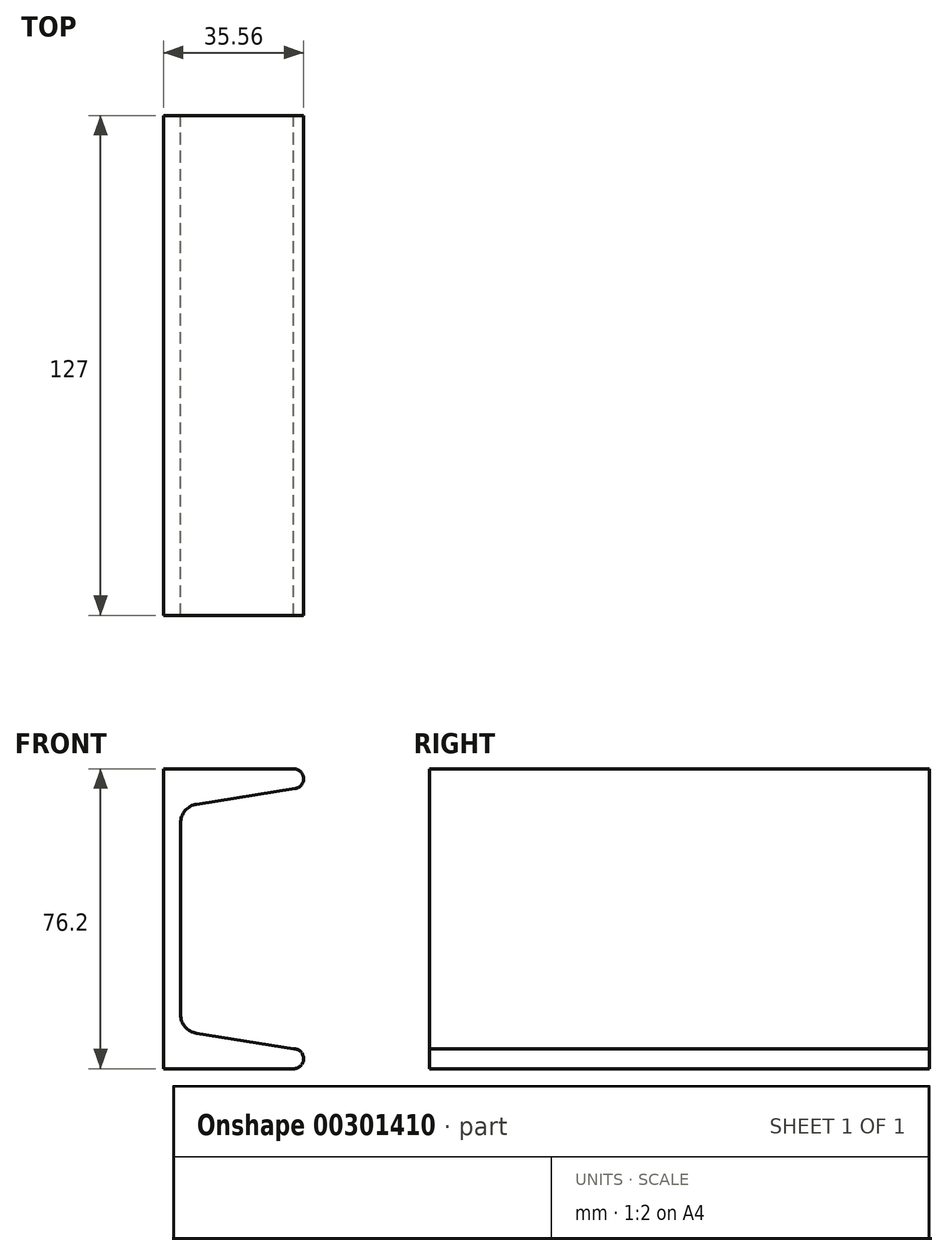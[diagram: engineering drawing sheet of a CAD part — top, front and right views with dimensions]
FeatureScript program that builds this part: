
annotation { "Feature Type Name" : "Feature", "Feature Type Description" : "" }
export const myFeature = defineFeature(function(context is Context, id is Id, definition is map)
    precondition{}
    {
        {
            var Q0;
            Q0=qCreatedBy(makeId("Front.planeOp"),FACE);
            var sketch = newSketch(context, id + "F0", { "sketchPlane" : qUnion([Q0])});
            skLineSegment(sketch, "E0", {"start": v(0, 0) * mm, "end": v(0, 76.2) * mm});
            skLineSegment(sketch, "E1", {"start": v(0, 76.2) * mm, "end": v(33.02, 76.2) * mm});
            skLineSegment(sketch, "E2", {"start": v(0, 0) * mm, "end": v(33.02, 0) * mm});
            skArc(sketch, "E3", {"start": v(33.02, 76.2) * mm, "mid": v(35.55, 73.86) * mm, "end": v(33.42, 71.15) * mm});
            skArc(sketch, "E4", {"start": v(33.02, 0) * mm, "mid": v(35.56, 2.54) * mm, "end": v(33.02, 5.08) * mm});
            skLineSegment(sketch, "E5", {"start": v(33.42, 71.15) * mm, "end": v(8.41, 67.2) * mm});
            skArc(sketch, "E6", {"start": v(8.41, 67.2) * mm, "mid": v(5.48, 65.55) * mm, "end": v(4.32, 62.4) * mm});
            skLineSegment(sketch, "E7", {"start": v(4.32, 62.4) * mm, "end": v(4.32, 13.77) * mm});
            skArc(sketch, "E8", {"start": v(4.32, 13.77) * mm, "mid": v(5.48, 10.62) * mm, "end": v(8.41, 8.98) * mm});
            skLineSegment(sketch, "E9", {"start": v(33.02, 5.08) * mm, "end": v(8.41, 8.98) * mm});
            skSolve(sketch);
        }
        {
            var Q0;
            Q0=makeQuery(id+"F0.imprint","IMPRINT",FACE,{"disambiguationData":[TD([[makeQuery(id+"F0.imprint","IMPRINT",EDGE,{"derivedFrom":sQuery(id+"F0.wireOp",EDGE,"E0")}),-1.0]])]});
            extrude(context, id + "F1", {"entities" : qUnion([Q0]), "endBound" : BoundingType.SYMMETRIC, "depth" : 127 * mm});
        }
    });
